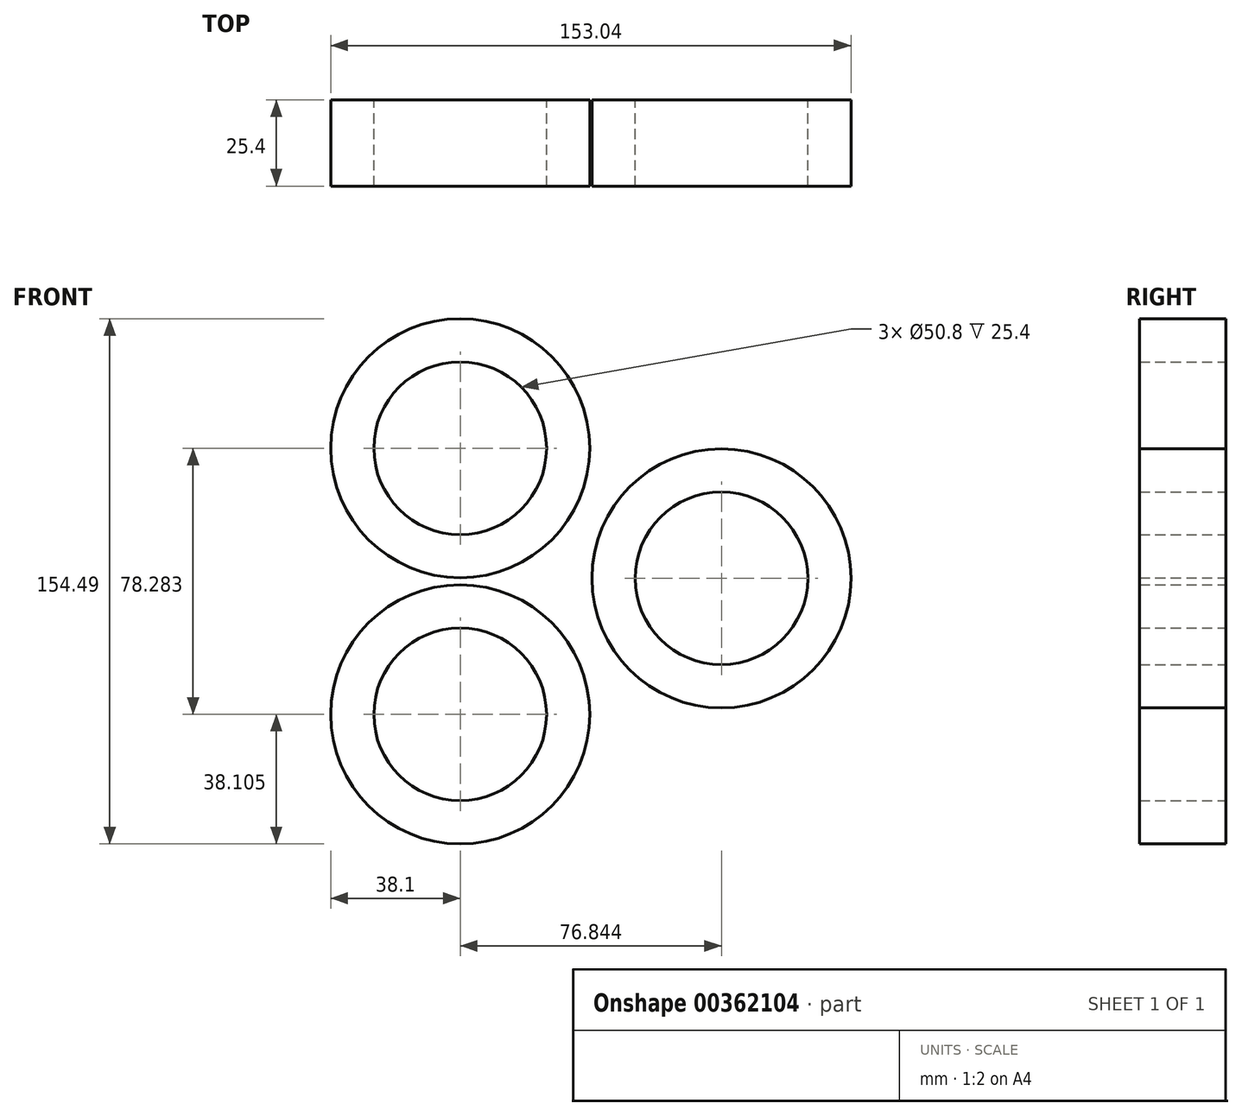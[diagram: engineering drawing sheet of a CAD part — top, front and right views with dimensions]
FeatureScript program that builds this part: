
annotation { "Feature Type Name" : "Feature", "Feature Type Description" : "" }
export const myFeature = defineFeature(function(context is Context, id is Id, definition is map)
    precondition{}
    {
        {
            var Q0;
            Q0=qCreatedBy(makeId("Front.planeOp"),FACE);
            var sketch = newSketch(context, id + "F0", { "sketchPlane" : qUnion([Q0])});
            skCircle(sketch, "E0", {"center": v(0, 38.28) * mm, "radius": 38.1 * mm});
            skCircle(sketch, "E1", {"center": v(0, 38.28) * mm, "radius": 25.4 * mm});
            skCircle(sketch, "E2", {"center": v(0, -40) * mm, "radius": 38.1 * mm});
            skCircle(sketch, "E3", {"center": v(0, -40) * mm, "radius": 25.4 * mm});
            skCircle(sketch, "E4", {"center": v(76.84, 0) * mm, "radius": 25.4 * mm});
            skCircle(sketch, "E5", {"center": v(76.84, 0) * mm, "radius": 38.1 * mm});
            skSolve(sketch);
        }
        {
            var Q0;
            Q0 = qSketchRegion(id + "F0", true);
            extrude(context, id + "F1", {"entities" : qUnion([Q0]), "depth" : 25.4 * mm});
        }
    });
